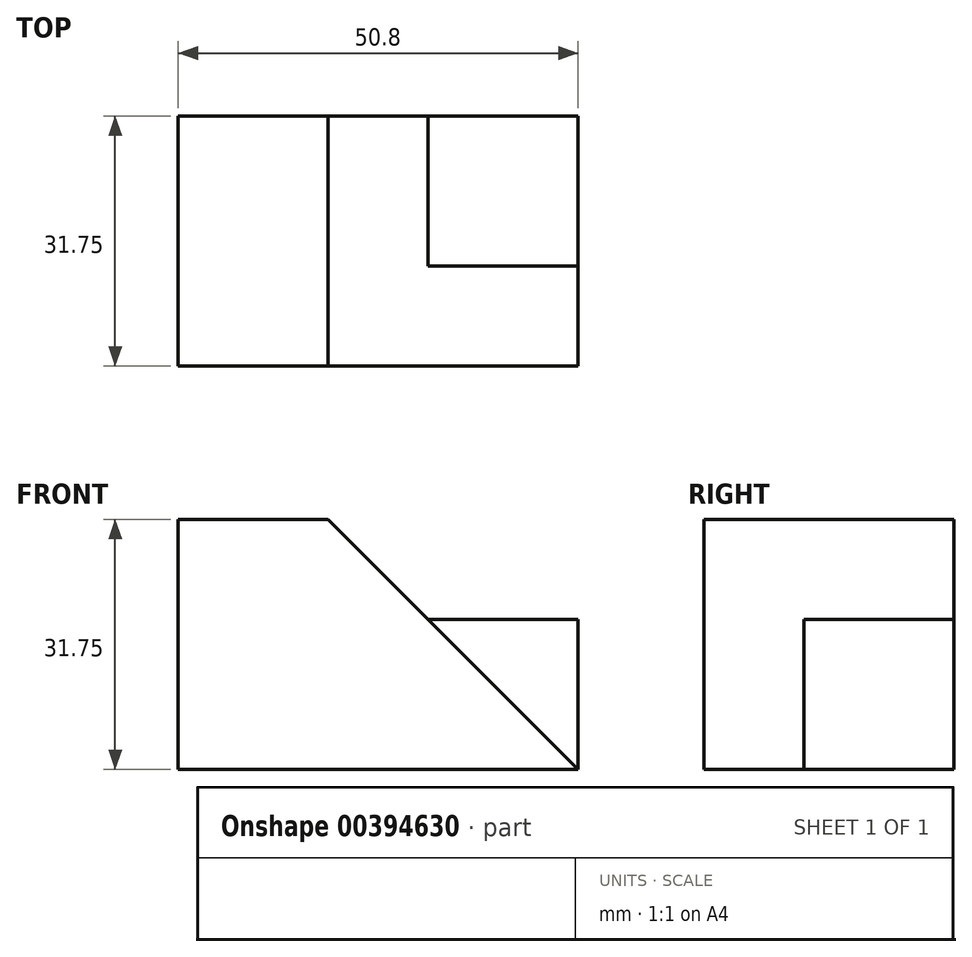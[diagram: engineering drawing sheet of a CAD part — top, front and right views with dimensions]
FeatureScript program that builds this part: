
annotation { "Feature Type Name" : "Feature", "Feature Type Description" : "" }
export const myFeature = defineFeature(function(context is Context, id is Id, definition is map)
    precondition{}
    {
        {
            var Q0;
            Q0=qCreatedBy(makeId("Front.planeOp"),FACE);
            var sketch = newSketch(context, id + "F0", { "sketchPlane" : qUnion([Q0])});
            skLineSegment(sketch, "E0", {"start": v(0, 0) * mm, "end": v(0, 31.75) * mm});
            skLineSegment(sketch, "E1", {"start": v(0, 31.75) * mm, "end": v(19.05, 31.75) * mm});
            skLineSegment(sketch, "E2", {"start": v(0, 0) * mm, "end": v(50.8, 0) * mm});
            skLineSegment(sketch, "E3", {"start": v(50.8, 0) * mm, "end": v(19.05, 31.75) * mm});
            skSolve(sketch);
        }
        {
            var Q0;
            Q0 = qSketchRegion(id + "F0", true);
            extrude(context, id + "F1", {"entities" : qUnion([Q0]), "depth" : 31.75 * mm});
        }
        {
            var Q0;
            Q0=qCreatedBy(makeId("Front.planeOp"),FACE);
            var sketch = newSketch(context, id + "F2", { "sketchPlane" : qUnion([Q0])});
            skLineSegment(sketch, "E4.0.0", {"start": v(0, 0) * mm, "end": v(50.8, 0) * mm});
            skLineSegment(sketch, "E4.0.1", {"start": v(50.8, 0) * mm, "end": v(19.05, 31.75) * mm});
            skLineSegment(sketch, "E4.0.2", {"start": v(19.05, 31.75) * mm, "end": v(0, 31.75) * mm});
            skLineSegment(sketch, "E4.0.3", {"start": v(0, 31.75) * mm, "end": v(0, 0) * mm});
            skLineSegment(sketch, "E5", {"start": v(50.8, 0) * mm, "end": v(50.8, 19.05) * mm});
            skLineSegment(sketch, "E6", {"start": v(50.8, 19.05) * mm, "end": v(31.75, 19.05) * mm});
            skSolve(sketch);
        }
        {
            var Q0;
            Q0 = qSketchRegion(id + "F2", true);
            extrude(context, id + "F3", {"entities" : qUnion([Q0]), "operationType" : NewBodyOperationType.ADD, "depth" : 19.05 * mm});
        }
    });
